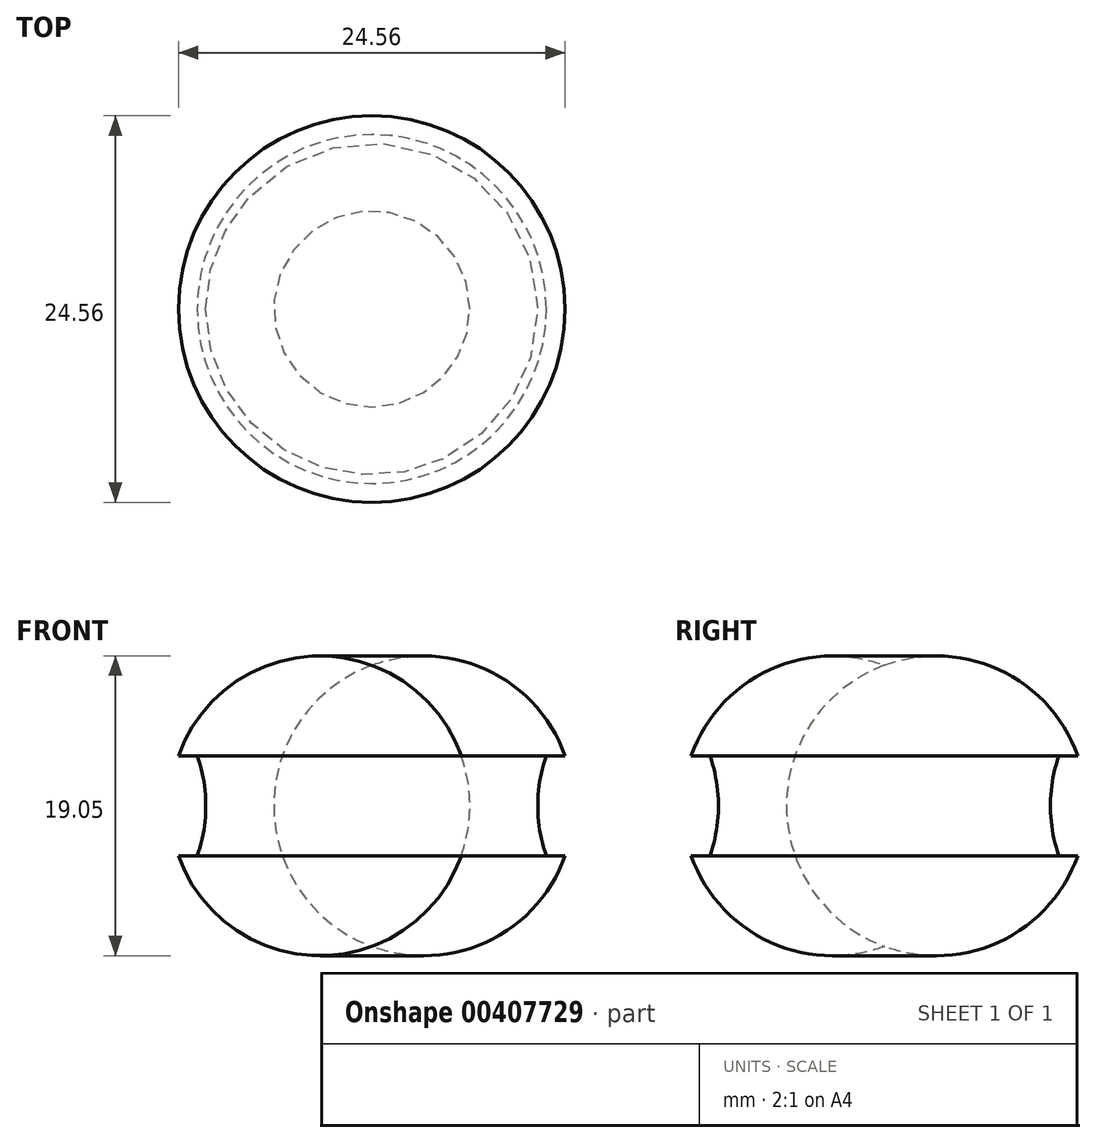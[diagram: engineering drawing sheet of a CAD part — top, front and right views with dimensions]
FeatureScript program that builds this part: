
annotation { "Feature Type Name" : "Feature", "Feature Type Description" : "" }
export const myFeature = defineFeature(function(context is Context, id is Id, definition is map)
    precondition{}
    {
        {
            var Q0;
            Q0=qCreatedBy(makeId("Front.planeOp"),FACE);
            var sketch = newSketch(context, id + "F0", { "sketchPlane" : qUnion([Q0])});
            skLineSegment(sketch, "E0", {"start": v(0, 0) * mm, "end": v(0, 13.64) * mm, "construction": true});
            skLineSegment(sketch, "E1", {"start": v(-15.08, 3.17) * mm, "end": v(-6.35, 3.17) * mm, "construction": true});
            skLineSegment(sketch, "E2", {"start": v(-11.09, 0) * mm, "end": v(-12.28, 0) * mm});
            skLineSegment(sketch, "E3.MirrorCS", {"start": v(-11.09, 6.35) * mm, "end": v(-12.28, 6.35) * mm});
            skArc(sketch, "E4", {"start": v(-12.28, 6.35) * mm, "mid": v(-12.82, 3.17) * mm, "end": v(-12.28, 0) * mm});
            skArc(sketch, "E5.trimOffspring", {"start": v(-11.09, 0) * mm, "mid": v(-10.54, 3.18) * mm, "end": v(-11.09, 6.35) * mm});
            skSolve(sketch);
        }
        {
            var Q0;
            Q0 = qSketchRegion(id + "F0", true);
            var Q1;
            Q1=sQuery(id+"F0.wireOp",EDGE,"E0");
            revolve(context, id + "F1", {"entities" : qUnion([Q0]), "axis" : qUnion([Q1]), "revolveType" : RevolveType.FULL});
        }
    });
